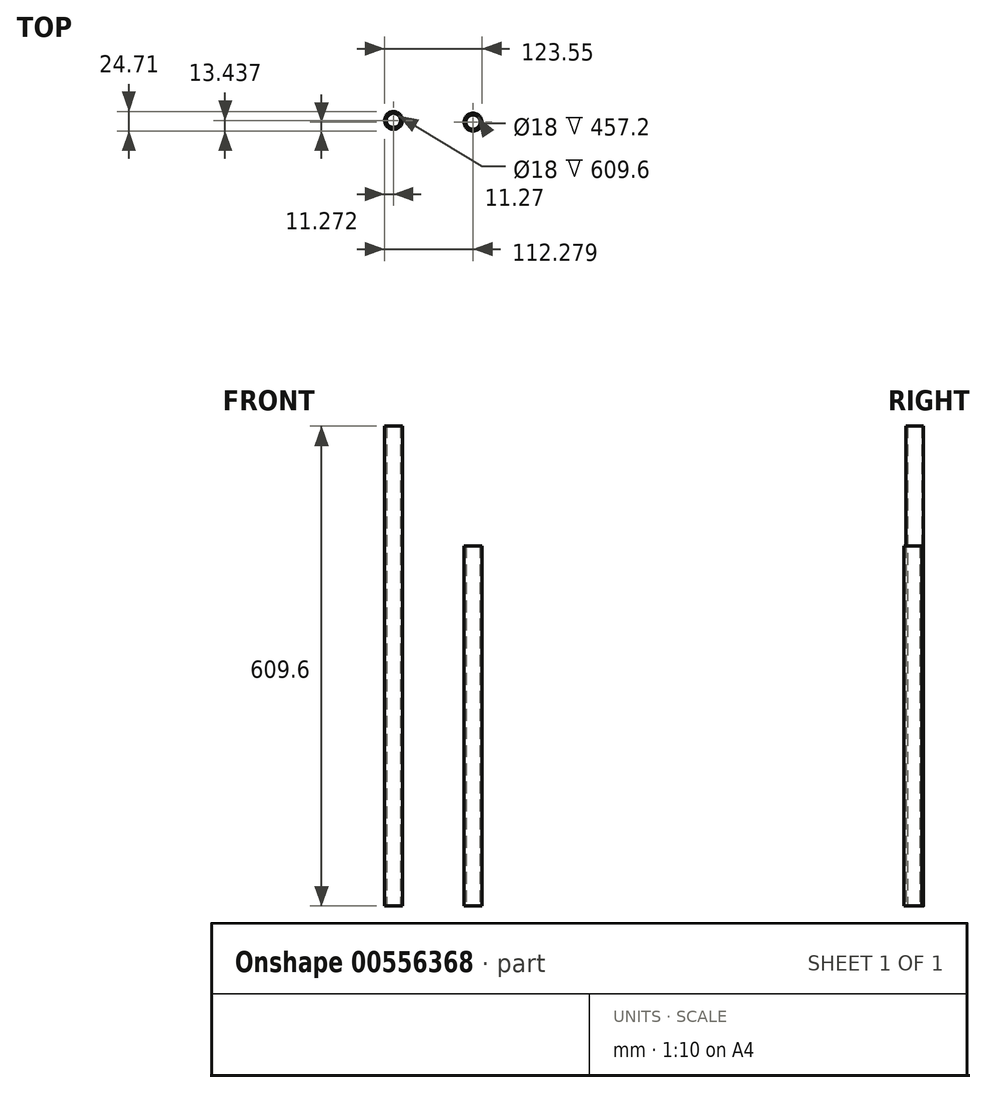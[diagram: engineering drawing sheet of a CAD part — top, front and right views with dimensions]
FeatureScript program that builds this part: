
annotation { "Feature Type Name" : "Feature", "Feature Type Description" : "" }
export const myFeature = defineFeature(function(context is Context, id is Id, definition is map)
    precondition{}
    {
        {
            var Q0;
            Q0=qCreatedBy(makeId("Top.planeOp"),FACE);
            var sketch = newSketch(context, id + "F0", { "sketchPlane" : qUnion([Q0])});
            skCircle(sketch, "E0", {"center": v(-51.07, 30.87) * mm, "radius": 11.27 * mm});
            skCircle(sketch, "E1", {"center": v(49.94, 28.7) * mm, "radius": 9 * mm});
            skCircle(sketch, "E2", {"center": v(-51.07, 30.87) * mm, "radius": 9 * mm});
            skCircle(sketch, "E3", {"center": v(49.94, 28.7) * mm, "radius": 11.27 * mm});
            skSolve(sketch);
        }
        {
            var Q0;
            Q0=makeQuery(id+"F0.imprint","IMPRINT",FACE,{"disambiguationData":[TD([[makeQuery(id+"F0.imprint","IMPRINT",EDGE,{"derivedFrom":sQuery(id+"F0.wireOp",EDGE,"E0")}),1.0]])]});
            extrude(context, id + "F1", {"entities" : qUnion([Q0]), "depth" : 609.6 * mm, "offsetDistance" : 25 * mm});
        }
        {
            var Q0;
            Q0=makeQuery(id+"F0.imprint","IMPRINT",FACE,{"disambiguationData":[TD([[makeQuery(id+"F0.imprint","IMPRINT",EDGE,{"derivedFrom":sQuery(id+"F0.wireOp",EDGE,"E1")}),-1.0]])]});
            extrude(context, id + "F2", {"entities" : qUnion([Q0]), "depth" : 457.2 * mm, "offsetDistance" : 25 * mm});
        }
    });
